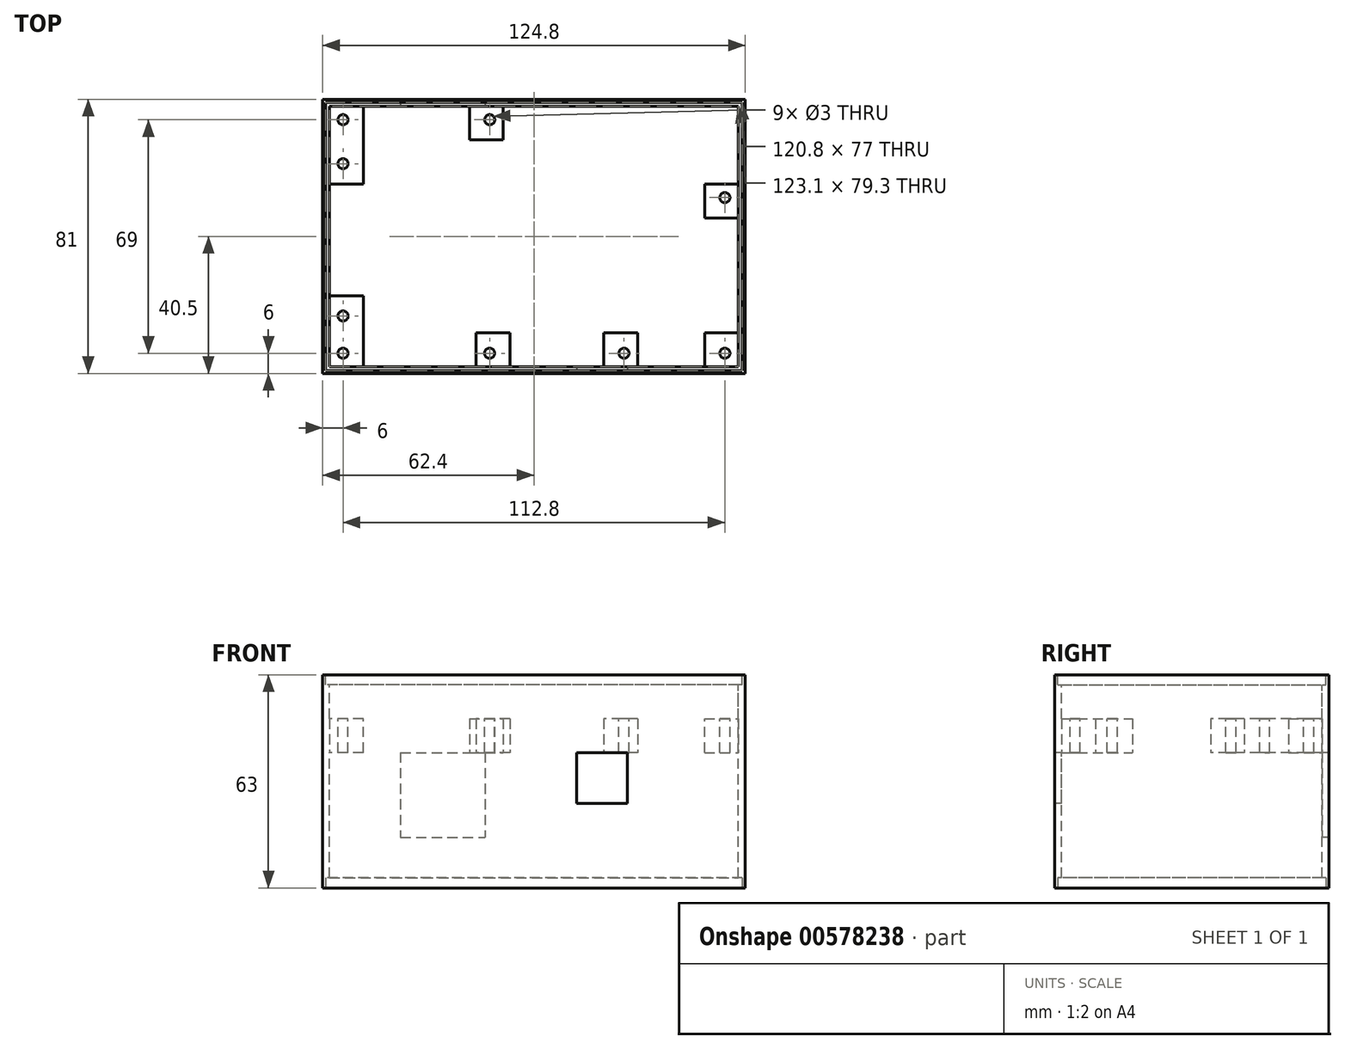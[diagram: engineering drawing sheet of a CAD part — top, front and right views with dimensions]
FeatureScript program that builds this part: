
annotation { "Feature Type Name" : "Feature", "Feature Type Description" : "" }
export const myFeature = defineFeature(function(context is Context, id is Id, definition is map)
    precondition{}
    {
        {
            var Q0;
            Q0=qCreatedBy(makeId("Top.planeOp"),FACE);
            var sketch = newSketch(context, id + "F0", { "sketchPlane" : qUnion([Q0])});
            skLineSegment(sketch, "E0.bottom", {"start": v(62.4, -40.5) * mm, "end": v(-62.4, -40.5) * mm});
            skLineSegment(sketch, "E0.top", {"start": v(62.4, 40.5) * mm, "end": v(-62.4, 40.5) * mm});
            skLineSegment(sketch, "E0.left", {"start": v(62.4, -40.5) * mm, "end": v(62.4, 40.5) * mm});
            skLineSegment(sketch, "E0.right", {"start": v(-62.4, -40.5) * mm, "end": v(-62.4, 40.5) * mm});
            skPoint(sketch, "E0.middle", {"position": v(0, 0) * mm});
            skSolve(sketch);
        }
        {
            var Q0;
            Q0 = qSketchRegion(id + "F0", true);
            var Q1;
            Q1=makeQuery(id+"F0.imprint","IMPRINT",FACE,{"disambiguationData":[TD([[makeQuery(id+"F0.imprint","IMPRINT",EDGE,{"derivedFrom":sQuery(id+"F0.wireOp",EDGE,"E0.bottom")}),-1.0]])]});
            extrude(context, id + "F1", {"entities" : qUnion([Q0, Q1]), "depth" : 63 * mm, "offsetDistance" : 25 * mm});
        }
        {
            var Q0;
            Q0=makeQuery(id+"F1.opExtrude","CAP_FACE",FACE,{"disambiguationData":[OSD([sQuery(id+"F0.wireOp",EDGE,"E0.bottom"),sQuery(id+"F0.wireOp",EDGE,"E0.top"),sQuery(id+"F0.wireOp",EDGE,"E0.left"),sQuery(id+"F0.wireOp",EDGE,"E0.right")])],"isStart":false});
            var sketch = newSketch(context, id + "F2", { "sketchPlane" : qUnion([Q0])});
            skLineSegment(sketch, "E1.bottom", {"start": v(61.55, -39.65) * mm, "end": v(-61.55, -39.65) * mm});
            skLineSegment(sketch, "E1.top", {"start": v(61.55, 39.65) * mm, "end": v(-61.55, 39.65) * mm});
            skLineSegment(sketch, "E1.left", {"start": v(61.55, -39.65) * mm, "end": v(61.55, 39.65) * mm});
            skLineSegment(sketch, "E1.right", {"start": v(-61.55, -39.65) * mm, "end": v(-61.55, 39.65) * mm});
            skPoint(sketch, "E1.middle", {"position": v(0, 0) * mm});
            skSolve(sketch);
        }
        {
            var Q0;
            Q0=makeQuery(id+"F2.imprint","IMPRINT",FACE,{"disambiguationData":[TD([[makeQuery(id+"F2.imprint","IMPRINT",EDGE,{"derivedFrom":sQuery(id+"F2.wireOp",EDGE,"E1.bottom")}),-1.0]])]});
            extrude(context, id + "F3", {"entities" : qUnion([Q0]), "operationType" : NewBodyOperationType.REMOVE, "oppositeDirection" : true, "depth" : 3 * mm, "offsetDistance" : 25 * mm});
        }
        {
            var Q0;
            Q0=makeQuery(id+"F1.opExtrude","CAP_FACE",FACE,{"disambiguationData":[OSD([sQuery(id+"F0.wireOp",EDGE,"E0.bottom"),sQuery(id+"F0.wireOp",EDGE,"E0.top"),sQuery(id+"F0.wireOp",EDGE,"E0.left"),sQuery(id+"F0.wireOp",EDGE,"E0.right")])],"isStart":true});
            var sketch = newSketch(context, id + "F4", { "sketchPlane" : qUnion([Q0])});
            skLineSegment(sketch, "E2.bottom", {"start": v(61.55, -39.65) * mm, "end": v(-61.55, -39.65) * mm});
            skLineSegment(sketch, "E2.top", {"start": v(61.55, 39.65) * mm, "end": v(-61.55, 39.65) * mm});
            skLineSegment(sketch, "E2.left", {"start": v(61.55, -39.65) * mm, "end": v(61.55, 39.65) * mm});
            skLineSegment(sketch, "E2.right", {"start": v(-61.55, -39.65) * mm, "end": v(-61.55, 39.65) * mm});
            skPoint(sketch, "E2.middle", {"position": v(0, 0) * mm});
            skSolve(sketch);
        }
        {
            var Q0;
            Q0=makeQuery(id+"F4.imprint","IMPRINT",FACE,{"disambiguationData":[TD([[makeQuery(id+"F4.imprint","IMPRINT",EDGE,{"derivedFrom":sQuery(id+"F4.wireOp",EDGE,"E2.bottom")}),-1.0]])]});
            extrude(context, id + "F5", {"entities" : qUnion([Q0]), "operationType" : NewBodyOperationType.REMOVE, "oppositeDirection" : true, "depth" : 3 * mm, "offsetDistance" : 25 * mm});
        }
        {
            var Q0;
            Q0=makeQuery(id+"F3.boolean.opBoolean","COPY",FACE,{"derivedFrom":makeQuery(id+"F3.opExtrude","CAP_FACE",FACE,{"disambiguationData":[OSD([sQuery(id+"F2.wireOp",EDGE,"E1.bottom"),sQuery(id+"F2.wireOp",EDGE,"E1.top"),sQuery(id+"F2.wireOp",EDGE,"E1.left"),sQuery(id+"F2.wireOp",EDGE,"E1.right")])],"isStart":false})});
            var sketch = newSketch(context, id + "F6", { "sketchPlane" : qUnion([Q0])});
            skLineSegment(sketch, "E3.bottom", {"start": v(60.4, -38.5) * mm, "end": v(-60.4, -38.5) * mm});
            skLineSegment(sketch, "E3.top", {"start": v(60.4, 38.5) * mm, "end": v(-60.4, 38.5) * mm});
            skLineSegment(sketch, "E3.left", {"start": v(60.4, -38.5) * mm, "end": v(60.4, 38.5) * mm});
            skLineSegment(sketch, "E3.right", {"start": v(-60.4, -38.5) * mm, "end": v(-60.4, 38.5) * mm});
            skPoint(sketch, "E3.middle", {"position": v(0, 0) * mm});
            skSolve(sketch);
        }
        {
            var Q0;
            Q0=makeQuery(id+"F6.imprint","IMPRINT",FACE,{"disambiguationData":[TD([[makeQuery(id+"F6.imprint","IMPRINT",EDGE,{"derivedFrom":sQuery(id+"F6.wireOp",EDGE,"E3.bottom")}),-1.0]])]});
            extrude(context, id + "F7", {"entities" : qUnion([Q0]), "operationType" : NewBodyOperationType.REMOVE, "endBound" : BoundingType.THROUGH_ALL, "oppositeDirection" : true, "depth" : 25 * mm, "offsetDistance" : 25 * mm});
        }
        {
            var Q0;
            Q0=makeQuery(id+"F7.boolean.opBoolean","COPY",FACE,{"derivedFrom":makeQuery(id+"F7.opExtrude","SWEPT_FACE",FACE,{"disambiguationData":[OSD([sQuery(id+"F6.wireOp",EDGE,"E3.right")])]})});
            var sketch = newSketch(context, id + "F8", { "sketchPlane" : qUnion([Q0])});
            skLineSegment(sketch, "E4.bottom", {"start": v(-38.5, 50) * mm, "end": v(-17.5, 50) * mm});
            skLineSegment(sketch, "E4.top", {"start": v(-38.5, 40) * mm, "end": v(-17.5, 40) * mm});
            skLineSegment(sketch, "E4.left", {"start": v(-38.5, 50) * mm, "end": v(-38.5, 40) * mm});
            skLineSegment(sketch, "E4.right", {"start": v(-17.5, 50) * mm, "end": v(-17.5, 40) * mm});
            skSolve(sketch);
        }
        {
            var Q0;
            Q0 = qSketchRegion(id + "F8", true);
            extrude(context, id + "F9", {"entities" : qUnion([Q0]), "operationType" : NewBodyOperationType.ADD, "depth" : 10 * mm, "offsetDistance" : 25 * mm});
        }
        {
            var Q0;
            Q0=makeQuery(id+"F7.boolean.opBoolean","COPY",FACE,{"derivedFrom":makeQuery(id+"F7.opExtrude","SWEPT_FACE",FACE,{"disambiguationData":[OSD([sQuery(id+"F6.wireOp",EDGE,"E3.right")])]})});
            var sketch = newSketch(context, id + "F10", { "sketchPlane" : qUnion([Q0])});
            skLineSegment(sketch, "E5.bottom", {"start": v(38.5, 50) * mm, "end": v(15.5, 50) * mm});
            skLineSegment(sketch, "E5.top", {"start": v(38.5, 40) * mm, "end": v(15.5, 40) * mm});
            skLineSegment(sketch, "E5.left", {"start": v(38.5, 50) * mm, "end": v(38.5, 40) * mm});
            skLineSegment(sketch, "E5.right", {"start": v(15.5, 50) * mm, "end": v(15.5, 40) * mm});
            skSolve(sketch);
        }
        {
            var Q0;
            Q0 = qSketchRegion(id + "F10", true);
            extrude(context, id + "F11", {"entities" : qUnion([Q0]), "operationType" : NewBodyOperationType.ADD, "depth" : 10 * mm, "offsetDistance" : 25 * mm});
        }
        {
            var Q0;
            Q0=makeQuery(id+"F7.boolean.opBoolean","COPY",FACE,{"derivedFrom":makeQuery(id+"F7.opExtrude","SWEPT_FACE",FACE,{"disambiguationData":[OSD([sQuery(id+"F6.wireOp",EDGE,"E3.left")])]})});
            var sketch = newSketch(context, id + "F12", { "sketchPlane" : qUnion([Q0])});
            skLineSegment(sketch, "E6.bottom", {"start": v(38.5, 50) * mm, "end": v(28.5, 50) * mm});
            skLineSegment(sketch, "E6.top", {"start": v(38.5, 40) * mm, "end": v(28.5, 40) * mm});
            skLineSegment(sketch, "E6.left", {"start": v(38.5, 50) * mm, "end": v(38.5, 40) * mm});
            skLineSegment(sketch, "E6.right", {"start": v(28.5, 50) * mm, "end": v(28.5, 40) * mm});
            skSolve(sketch);
        }
        {
            var Q0;
            Q0 = qSketchRegion(id + "F12", true);
            extrude(context, id + "F13", {"entities" : qUnion([Q0]), "operationType" : NewBodyOperationType.ADD, "depth" : 10 * mm, "offsetDistance" : 25 * mm});
        }
        {
            var Q0;
            Q0=makeQuery(id+"F7.boolean.opBoolean","COPY",FACE,{"derivedFrom":makeQuery(id+"F7.opExtrude","SWEPT_FACE",FACE,{"disambiguationData":[OSD([sQuery(id+"F6.wireOp",EDGE,"E3.left")])]})});
            var sketch = newSketch(context, id + "F14", { "sketchPlane" : qUnion([Q0])});
            skLineSegment(sketch, "E7.bottom", {"start": v(-15.5, 50) * mm, "end": v(-5.5, 50) * mm});
            skLineSegment(sketch, "E7.top", {"start": v(-15.5, 40) * mm, "end": v(-5.5, 40) * mm});
            skLineSegment(sketch, "E7.left", {"start": v(-15.5, 50) * mm, "end": v(-15.5, 40) * mm});
            skLineSegment(sketch, "E7.right", {"start": v(-5.5, 50) * mm, "end": v(-5.5, 40) * mm});
            skSolve(sketch);
        }
        {
            var Q0;
            Q0 = qSketchRegion(id + "F14", true);
            extrude(context, id + "F15", {"entities" : qUnion([Q0]), "operationType" : NewBodyOperationType.ADD, "depth" : 10 * mm, "offsetDistance" : 25 * mm});
        }
        {
            var Q0;
            Q0=makeQuery(id+"F7.boolean.opBoolean","COPY",FACE,{"derivedFrom":makeQuery(id+"F7.opExtrude","SWEPT_FACE",FACE,{"disambiguationData":[OSD([sQuery(id+"F6.wireOp",EDGE,"E3.bottom")])]})});
            var sketch = newSketch(context, id + "F16", { "sketchPlane" : qUnion([Q0])});
            skLineSegment(sketch, "E8.bottom", {"start": v(-30.6, 50) * mm, "end": v(-20.6, 50) * mm});
            skLineSegment(sketch, "E8.top", {"start": v(-30.6, 40) * mm, "end": v(-20.6, 40) * mm});
            skLineSegment(sketch, "E8.left", {"start": v(-30.6, 50) * mm, "end": v(-30.6, 40) * mm});
            skLineSegment(sketch, "E8.right", {"start": v(-20.6, 50) * mm, "end": v(-20.6, 40) * mm});
            skSolve(sketch);
        }
        {
            var Q0;
            Q0 = qSketchRegion(id + "F16", true);
            extrude(context, id + "F17", {"entities" : qUnion([Q0]), "operationType" : NewBodyOperationType.ADD, "depth" : 10 * mm, "offsetDistance" : 25 * mm});
        }
        {
            var Q0;
            Q0=makeQuery(id+"F7.boolean.opBoolean","COPY",FACE,{"derivedFrom":makeQuery(id+"F7.opExtrude","SWEPT_FACE",FACE,{"disambiguationData":[OSD([sQuery(id+"F6.wireOp",EDGE,"E3.bottom")])]})});
            var sketch = newSketch(context, id + "F18", { "sketchPlane" : qUnion([Q0])});
            skLineSegment(sketch, "E9.bottom", {"start": v(7.1, 50) * mm, "end": v(17.1, 50) * mm});
            skLineSegment(sketch, "E9.top", {"start": v(7.1, 40) * mm, "end": v(17.1, 40) * mm});
            skLineSegment(sketch, "E9.left", {"start": v(7.1, 50) * mm, "end": v(7.1, 40) * mm});
            skLineSegment(sketch, "E9.right", {"start": v(17.1, 50) * mm, "end": v(17.1, 40) * mm});
            skSolve(sketch);
        }
        {
            var Q0;
            Q0 = qSketchRegion(id + "F18", true);
            extrude(context, id + "F19", {"entities" : qUnion([Q0]), "operationType" : NewBodyOperationType.ADD, "depth" : 10 * mm, "offsetDistance" : 25 * mm});
        }
        {
            var Q0;
            Q0=makeQuery(id+"F7.boolean.opBoolean","COPY",FACE,{"derivedFrom":makeQuery(id+"F7.opExtrude","SWEPT_FACE",FACE,{"disambiguationData":[OSD([sQuery(id+"F6.wireOp",EDGE,"E3.top")])]})});
            var sketch = newSketch(context, id + "F20", { "sketchPlane" : qUnion([Q0])});
            skLineSegment(sketch, "E10.bottom", {"start": v(-19.06, 50) * mm, "end": v(-9.06, 50) * mm});
            skLineSegment(sketch, "E10.top", {"start": v(-19.06, 40) * mm, "end": v(-9.06, 40) * mm});
            skLineSegment(sketch, "E10.left", {"start": v(-19.06, 50) * mm, "end": v(-19.06, 40) * mm});
            skLineSegment(sketch, "E10.right", {"start": v(-9.06, 50) * mm, "end": v(-9.06, 40) * mm});
            skSolve(sketch);
        }
        {
            var Q0;
            Q0 = qSketchRegion(id + "F20", true);
            extrude(context, id + "F21", {"entities" : qUnion([Q0]), "operationType" : NewBodyOperationType.ADD, "depth" : 10 * mm, "offsetDistance" : 25 * mm});
        }
        {
            var Q0;
            Q0=makeQuery(id+"F9.opExtrude","SWEPT_FACE",FACE,{"disambiguationData":[OSD([sQuery(id+"F8.wireOp",EDGE,"E4.bottom")])]});
            var sketch = newSketch(context, id + "F22", { "sketchPlane" : qUnion([Q0])});
            skCircle(sketch, "E11", {"center": v(-56.4, -34.5) * mm, "radius": 1.5 * mm});
            skSolve(sketch);
        }
        {
            var Q0;
            Q0 = qSketchRegion(id + "F22", true);
            extrude(context, id + "F23", {"entities" : qUnion([Q0]), "operationType" : NewBodyOperationType.REMOVE, "endBound" : BoundingType.THROUGH_ALL, "oppositeDirection" : true, "depth" : 25 * mm, "offsetDistance" : 25 * mm});
        }
        {
            var Q0;
            Q0=makeQuery(id+"F9.opExtrude","SWEPT_FACE",FACE,{"disambiguationData":[OSD([sQuery(id+"F8.wireOp",EDGE,"E4.bottom")])]});
            var sketch = newSketch(context, id + "F24", { "sketchPlane" : qUnion([Q0])});
            skCircle(sketch, "E12", {"center": v(-56.4, -23.5) * mm, "radius": 1.5 * mm});
            skSolve(sketch);
        }
        {
            var Q0;
            Q0 = qSketchRegion(id + "F24", true);
            extrude(context, id + "F25", {"entities" : qUnion([Q0]), "operationType" : NewBodyOperationType.REMOVE, "endBound" : BoundingType.THROUGH_ALL, "oppositeDirection" : true, "depth" : 25 * mm, "offsetDistance" : 25 * mm});
        }
        {
            var Q0;
            Q0=makeQuery(id+"F11.opExtrude","SWEPT_FACE",FACE,{"disambiguationData":[OSD([sQuery(id+"F10.wireOp",EDGE,"E5.bottom")])]});
            var sketch = newSketch(context, id + "F26", { "sketchPlane" : qUnion([Q0])});
            skCircle(sketch, "E13", {"center": v(-56.4, 34.5) * mm, "radius": 1.5 * mm});
            skSolve(sketch);
        }
        {
            var Q0;
            Q0 = qSketchRegion(id + "F26", true);
            extrude(context, id + "F27", {"entities" : qUnion([Q0]), "operationType" : NewBodyOperationType.REMOVE, "endBound" : BoundingType.THROUGH_ALL, "oppositeDirection" : true, "depth" : 25 * mm, "offsetDistance" : 25 * mm});
        }
        {
            var Q0;
            Q0=makeQuery(id+"F11.opExtrude","SWEPT_FACE",FACE,{"disambiguationData":[OSD([sQuery(id+"F10.wireOp",EDGE,"E5.bottom")])]});
            var sketch = newSketch(context, id + "F28", { "sketchPlane" : qUnion([Q0])});
            skCircle(sketch, "E14", {"center": v(-56.4, 21.5) * mm, "radius": 1.5 * mm});
            skSolve(sketch);
        }
        {
            var Q0;
            Q0 = qSketchRegion(id + "F28", true);
            extrude(context, id + "F29", {"entities" : qUnion([Q0]), "operationType" : NewBodyOperationType.REMOVE, "endBound" : BoundingType.THROUGH_ALL, "oppositeDirection" : true, "depth" : 25 * mm, "offsetDistance" : 25 * mm});
        }
        {
            var Q0;
            Q0=makeQuery(id+"F13.opExtrude","SWEPT_FACE",FACE,{"disambiguationData":[OSD([sQuery(id+"F12.wireOp",EDGE,"E6.bottom")])]});
            var sketch = newSketch(context, id + "F30", { "sketchPlane" : qUnion([Q0])});
            skCircle(sketch, "E15", {"center": v(56.4, -34.5) * mm, "radius": 1.5 * mm});
            skSolve(sketch);
        }
        {
            var Q0;
            Q0 = qSketchRegion(id + "F30", true);
            extrude(context, id + "F31", {"entities" : qUnion([Q0]), "operationType" : NewBodyOperationType.REMOVE, "endBound" : BoundingType.THROUGH_ALL, "oppositeDirection" : true, "depth" : 25 * mm, "offsetDistance" : 25 * mm});
        }
        {
            var Q0;
            Q0=makeQuery(id+"F15.opExtrude","SWEPT_FACE",FACE,{"disambiguationData":[OSD([sQuery(id+"F14.wireOp",EDGE,"E7.bottom")])]});
            var sketch = newSketch(context, id + "F32", { "sketchPlane" : qUnion([Q0])});
            skCircle(sketch, "E16", {"center": v(56.4, 11.5) * mm, "radius": 1.5 * mm});
            skSolve(sketch);
        }
        {
            var Q0;
            Q0 = qSketchRegion(id + "F32", true);
            extrude(context, id + "F33", {"entities" : qUnion([Q0]), "operationType" : NewBodyOperationType.REMOVE, "endBound" : BoundingType.THROUGH_ALL, "oppositeDirection" : true, "depth" : 25 * mm, "offsetDistance" : 25 * mm});
        }
        {
            var Q0;
            Q0=makeQuery(id+"F17.opExtrude","SWEPT_FACE",FACE,{"disambiguationData":[OSD([sQuery(id+"F16.wireOp",EDGE,"E8.bottom")])]});
            var sketch = newSketch(context, id + "F34", { "sketchPlane" : qUnion([Q0])});
            skCircle(sketch, "E17", {"center": v(26.6, -34.5) * mm, "radius": 1.5 * mm});
            skSolve(sketch);
        }
        {
            var Q0;
            Q0 = qSketchRegion(id + "F34", true);
            extrude(context, id + "F35", {"entities" : qUnion([Q0]), "operationType" : NewBodyOperationType.REMOVE, "endBound" : BoundingType.THROUGH_ALL, "oppositeDirection" : true, "depth" : 25 * mm, "offsetDistance" : 25 * mm});
        }
        {
            var Q0;
            Q0=makeQuery(id+"F19.opExtrude","SWEPT_FACE",FACE,{"disambiguationData":[OSD([sQuery(id+"F18.wireOp",EDGE,"E9.bottom")])]});
            var sketch = newSketch(context, id + "F36", { "sketchPlane" : qUnion([Q0])});
            skCircle(sketch, "E18", {"center": v(-13.1, -34.5) * mm, "radius": 1.5 * mm});
            skSolve(sketch);
        }
        {
            var Q0;
            Q0 = qSketchRegion(id + "F36", true);
            extrude(context, id + "F37", {"entities" : qUnion([Q0]), "operationType" : NewBodyOperationType.REMOVE, "endBound" : BoundingType.THROUGH_ALL, "oppositeDirection" : true, "depth" : 25 * mm, "offsetDistance" : 25 * mm});
        }
        {
            var Q0;
            Q0=makeQuery(id+"F21.opExtrude","SWEPT_FACE",FACE,{"disambiguationData":[OSD([sQuery(id+"F20.wireOp",EDGE,"E10.bottom")])]});
            var sketch = newSketch(context, id + "F38", { "sketchPlane" : qUnion([Q0])});
            skCircle(sketch, "E19", {"center": v(-13.06, 34.5) * mm, "radius": 1.5 * mm});
            skSolve(sketch);
        }
        {
            var Q0;
            Q0 = qSketchRegion(id + "F38", true);
            extrude(context, id + "F39", {"entities" : qUnion([Q0]), "operationType" : NewBodyOperationType.REMOVE, "endBound" : BoundingType.THROUGH_ALL, "oppositeDirection" : true, "depth" : 25 * mm, "offsetDistance" : 25 * mm});
        }
        {
            var Q0;
            Q0=makeQuery(id+"F7.boolean.opBoolean","COPY",FACE,{"derivedFrom":makeQuery(id+"F7.opExtrude","SWEPT_FACE",FACE,{"disambiguationData":[OSD([sQuery(id+"F6.wireOp",EDGE,"E3.top")])]})});
            var sketch = newSketch(context, id + "F40", { "sketchPlane" : qUnion([Q0])});
            skLineSegment(sketch, "E20.bottom", {"start": v(-39.4, 40) * mm, "end": v(-14.4, 40) * mm});
            skLineSegment(sketch, "E20.top", {"start": v(-39.4, 15) * mm, "end": v(-14.4, 15) * mm});
            skLineSegment(sketch, "E20.left", {"start": v(-39.4, 40) * mm, "end": v(-39.4, 15) * mm});
            skLineSegment(sketch, "E20.right", {"start": v(-14.4, 40) * mm, "end": v(-14.4, 15) * mm});
            skSolve(sketch);
        }
        {
            var Q0;
            Q0 = qSketchRegion(id + "F40", true);
            extrude(context, id + "F41", {"entities" : qUnion([Q0]), "operationType" : NewBodyOperationType.REMOVE, "endBound" : BoundingType.THROUGH_ALL, "oppositeDirection" : true, "depth" : 25 * mm, "offsetDistance" : 25 * mm});
        }
        {
            var Q0;
            Q0=makeQuery(id+"F1.opExtrude","SWEPT_FACE",FACE,{"disambiguationData":[OSD([sQuery(id+"F0.wireOp",EDGE,"E0.bottom")])]});
            var sketch = newSketch(context, id + "F42", { "sketchPlane" : qUnion([Q0])});
            skLineSegment(sketch, "E21.bottom", {"start": v(12.6, 40) * mm, "end": v(27.6, 40) * mm});
            skLineSegment(sketch, "E21.top", {"start": v(12.6, 25) * mm, "end": v(27.6, 25) * mm});
            skLineSegment(sketch, "E21.left", {"start": v(12.6, 40) * mm, "end": v(12.6, 25) * mm});
            skLineSegment(sketch, "E21.right", {"start": v(27.6, 40) * mm, "end": v(27.6, 25) * mm});
            skSolve(sketch);
        }
        {
            var Q0;
            Q0 = qSketchRegion(id + "F42", true);
            extrude(context, id + "F43", {"entities" : qUnion([Q0]), "operationType" : NewBodyOperationType.REMOVE, "oppositeDirection" : true, "depth" : 12 * mm, "offsetDistance" : 25 * mm});
        }
    });
